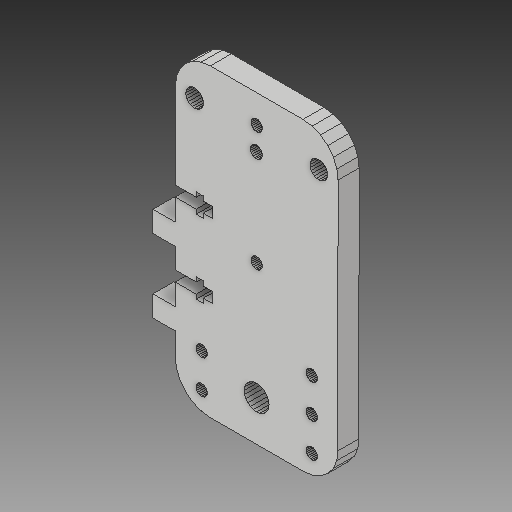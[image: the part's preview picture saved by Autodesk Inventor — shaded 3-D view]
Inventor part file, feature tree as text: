
AUTODESK INVENTOR PART (.ipt)
format: ipt  version: 2018 (Build 220112000, 112)  size: 586,752 bytes
history: native  units: mm
features: other x3, sketch x1
ambient origin geometry x8: Origin, YZ Plane, XZ Plane, XY Plane, X Axis, Y Axis, Z Axis, Center Point
bodies: Solid1 (feature_tree)
feature tree (4):
  other  "Hotend Rear Plate_MIR.ipt"
  other  "Solid1::Hotend Rear Plate_MIR.ipt"
  other  "TaggingFeature1"
  sketch  "Sketch1"  dims[d0=10.0mm]
